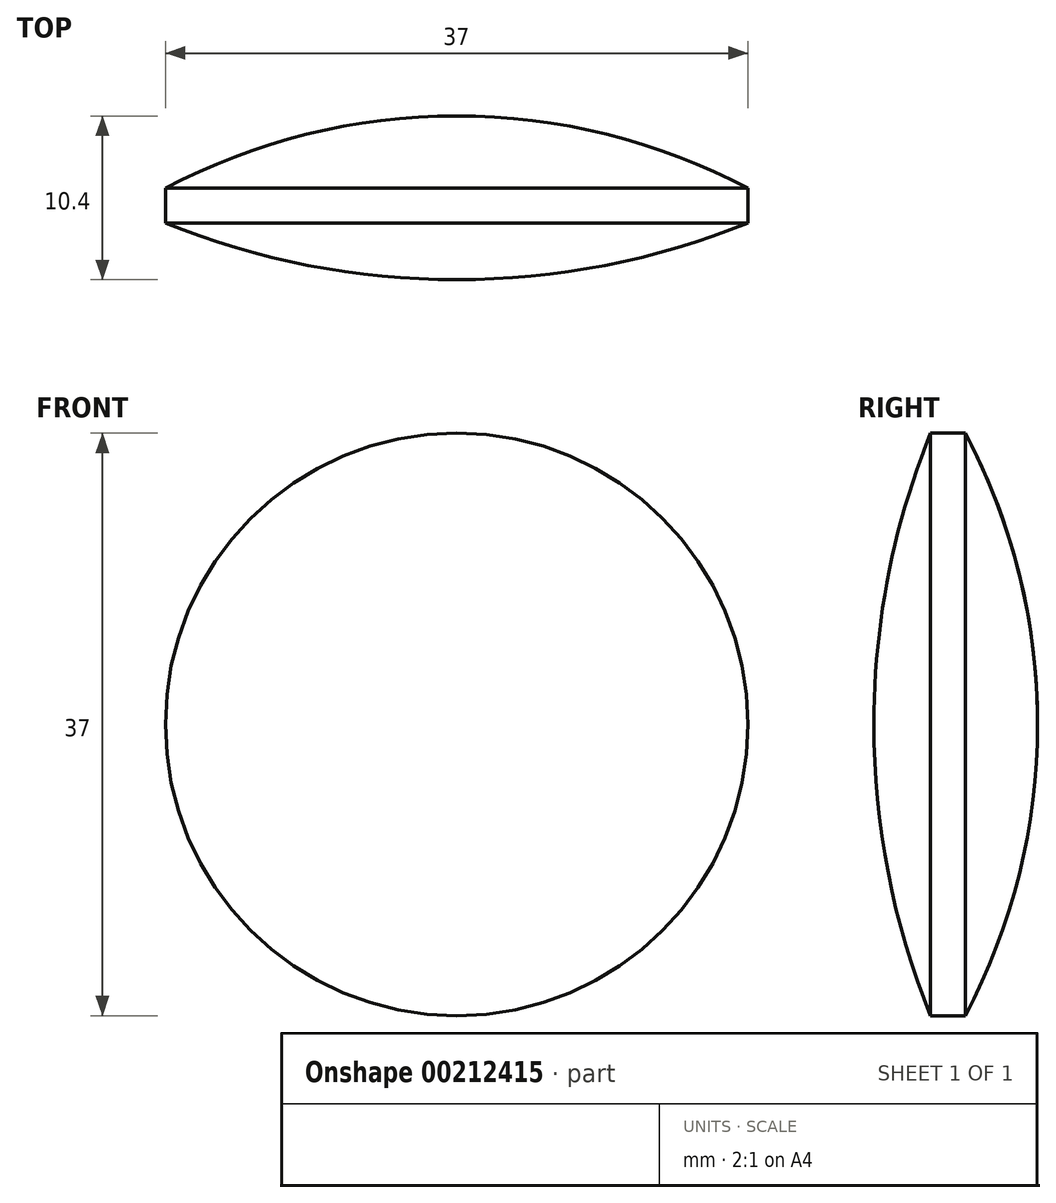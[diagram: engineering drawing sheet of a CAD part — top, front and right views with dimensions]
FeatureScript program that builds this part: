
annotation { "Feature Type Name" : "Feature", "Feature Type Description" : "" }
export const myFeature = defineFeature(function(context is Context, id is Id, definition is map)
    precondition{}
    {
        {
            var Q0;
            Q0=qCreatedBy(makeId("Right.planeOp"),FACE);
            var sketch = newSketch(context, id + "F0", { "sketchPlane" : qUnion([Q0])});
            skLineSegment(sketch, "E0.bottom", {"start": v(-1.1, 18.5) * mm, "end": v(1.1, 18.5) * mm});
            skLineSegment(sketch, "E0.left", {"start": v(-1.1, 18.5) * mm, "end": v(-1.1, -18.5) * mm, "construction": true});
            skLineSegment(sketch, "E0.right", {"start": v(1.1, 18.5) * mm, "end": v(1.1, -18.5) * mm, "construction": true});
            skArc(sketch, "E1", {"start": v(-1.1, 18.5) * mm, "mid": v(-3.8, 9.42) * mm, "end": v(-4.7, 0) * mm});
            skArc(sketch, "E2", {"start": v(5.7, 0) * mm, "mid": v(4.53, 9.53) * mm, "end": v(1.1, 18.5) * mm});
            skLineSegment(sketch, "E3", {"start": v(-4.7, 0) * mm, "end": v(5.7, 0) * mm});
            skSolve(sketch);
        }
        {
            var Q0;
            Q0 = qSketchRegion(id + "F0", true);
            var Q1;
            Q1=sQuery(id+"F0.wireOp",EDGE,"E3");
            revolve(context, id + "F1", {"entities" : qUnion([Q0]), "axis" : qUnion([Q1]), "revolveType" : RevolveType.FULL});
        }
    });
